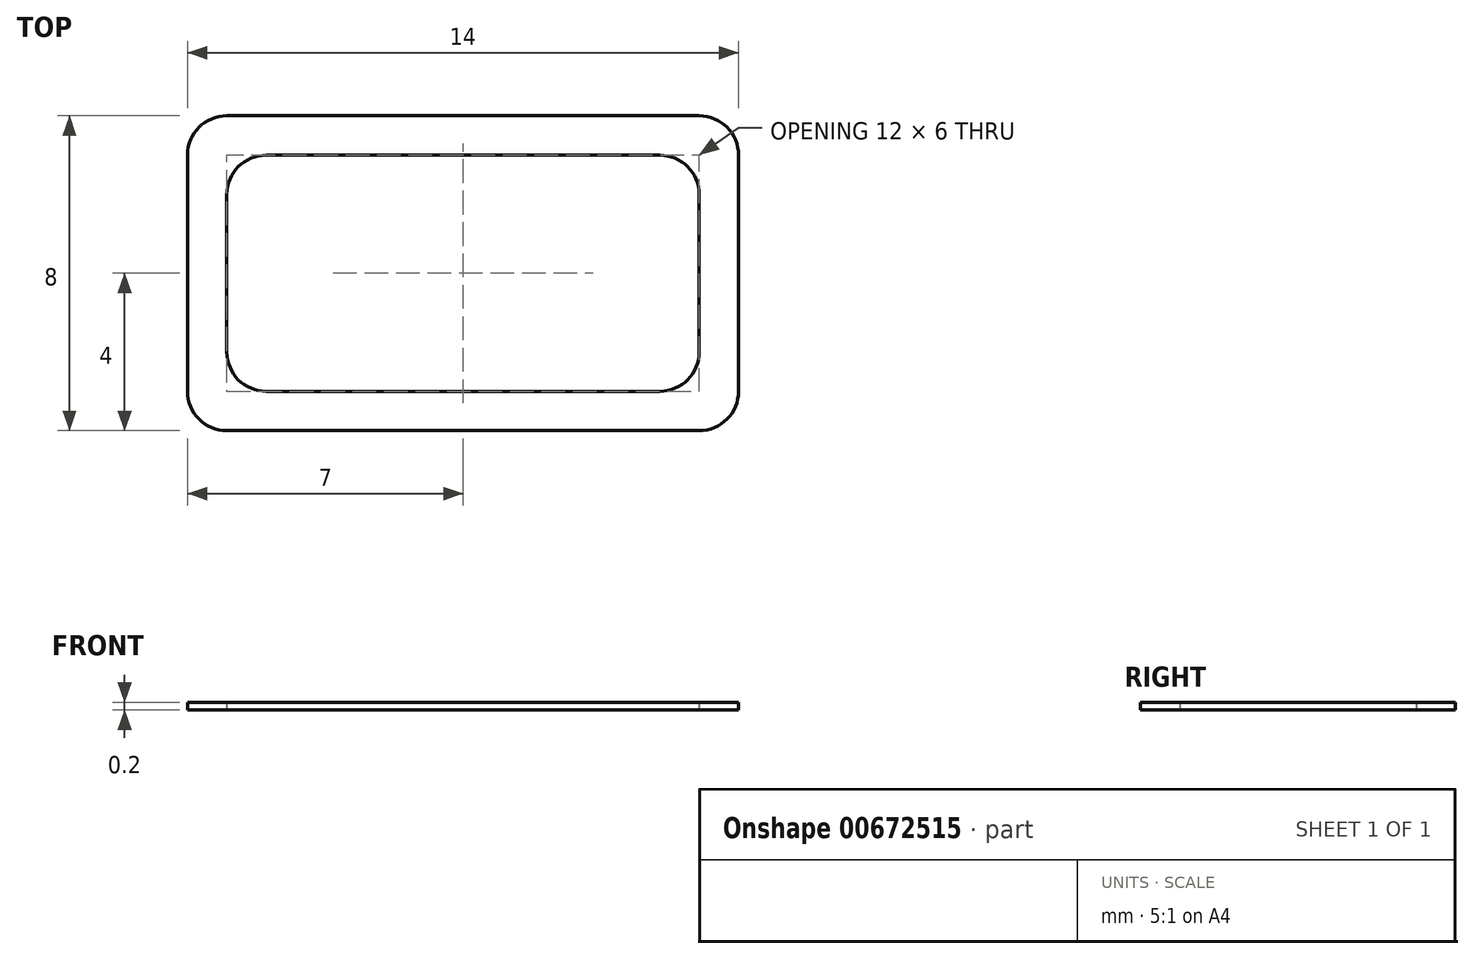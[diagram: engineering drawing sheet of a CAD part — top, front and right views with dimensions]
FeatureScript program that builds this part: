
annotation { "Feature Type Name" : "Feature", "Feature Type Description" : "" }
export const myFeature = defineFeature(function(context is Context, id is Id, definition is map)
    precondition{}
    {
        {
            var Q0;
            Q0=qCreatedBy(makeId("Top.planeOp"),FACE);
            var sketch = newSketch(context, id + "F0", { "sketchPlane" : qUnion([Q0])});
            skLineSegment(sketch, "E0.bottom", {"start": v(6, 4) * mm, "end": v(-6, 4) * mm});
            skLineSegment(sketch, "E0.top", {"start": v(6, -4) * mm, "end": v(-6, -4) * mm});
            skLineSegment(sketch, "E0.left", {"start": v(7, 3) * mm, "end": v(7, -3) * mm});
            skLineSegment(sketch, "E0.right", {"start": v(-7, 3) * mm, "end": v(-7, -3) * mm});
            skPoint(sketch, "E0.middle", {"position": v(0, 0) * mm});
            skPoint(sketch, "E1.visualSharp", {"position": v(-7, 4) * mm});
            skArc(sketch, "E1.filletArc", {"start": v(-6, 4) * mm, "mid": v(-6.7, 3.7) * mm, "end": v(-7, 3) * mm});
            skPoint(sketch, "E2.visualSharp", {"position": v(-7, -4) * mm});
            skArc(sketch, "E2.filletArc", {"start": v(-7, -3) * mm, "mid": v(-6.7, -3.7) * mm, "end": v(-6, -4) * mm});
            skPoint(sketch, "E3.visualSharp", {"position": v(7, 4) * mm});
            skArc(sketch, "E3.filletArc", {"start": v(7, 3) * mm, "mid": v(6.7, 3.7) * mm, "end": v(6, 4) * mm});
            skPoint(sketch, "E4.visualSharp", {"position": v(7, -4) * mm});
            skArc(sketch, "E4.filletArc", {"start": v(6, -4) * mm, "mid": v(6.7, -3.7) * mm, "end": v(7, -3) * mm});
            skSolve(sketch);
        }
        {
            var Q0;
            Q0=makeQuery(id+"F0.imprint","IMPRINT",FACE,{"disambiguationData":[TD([[makeQuery(id+"F0.imprint","IMPRINT",EDGE,{"derivedFrom":sQuery(id+"F0.wireOp",EDGE,"E0.bottom")}),1.0]])]});
            var sketch = newSketch(context, id + "F1", { "sketchPlane" : qUnion([Q0])});
            skLineSegment(sketch, "E5.bottom", {"start": v(-5, 3) * mm, "end": v(5, 3) * mm});
            skLineSegment(sketch, "E5.top", {"start": v(-5, -3) * mm, "end": v(5, -3) * mm});
            skLineSegment(sketch, "E5.left", {"start": v(-6, 2) * mm, "end": v(-6, -2) * mm});
            skLineSegment(sketch, "E5.right", {"start": v(6, 2) * mm, "end": v(6, -2) * mm});
            skPoint(sketch, "E5.middle", {"position": v(0, 0) * mm});
            skPoint(sketch, "E6.visualSharp", {"position": v(-6, 3) * mm});
            skArc(sketch, "E6.filletArc", {"start": v(-5, 3) * mm, "mid": v(-5.7, 2.7) * mm, "end": v(-6, 2) * mm});
            skPoint(sketch, "E7.visualSharp", {"position": v(-6, -3) * mm});
            skArc(sketch, "E7.filletArc", {"start": v(-6, -2) * mm, "mid": v(-5.7, -2.7) * mm, "end": v(-5, -3) * mm});
            skPoint(sketch, "E8.visualSharp", {"position": v(6, -3) * mm});
            skArc(sketch, "E8.filletArc", {"start": v(5, -3) * mm, "mid": v(5.7, -2.7) * mm, "end": v(6, -2) * mm});
            skPoint(sketch, "E9.visualSharp", {"position": v(6, 3) * mm});
            skArc(sketch, "E9.filletArc", {"start": v(6, 2) * mm, "mid": v(5.7, 2.7) * mm, "end": v(5, 3) * mm});
            skSolve(sketch);
        }
        {
            var Q0;
            Q0 = qSketchRegion(id + "F0", true);
            extrude(context, id + "F2", {"entities" : qUnion([Q0]), "depth" : 0.2 * mm, "offsetDistance" : 25 * mm});
        }
        {
            var Q0;
            Q0 = qSketchRegion(id + "F1", true);
            extrude(context, id + "F3", {"entities" : qUnion([Q0]), "operationType" : NewBodyOperationType.REMOVE, "depth" : 1 * mm, "offsetDistance" : 25 * mm});
        }
    });
